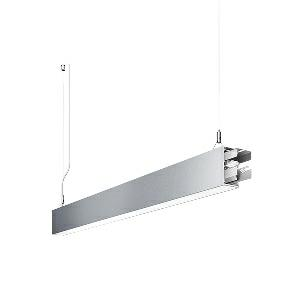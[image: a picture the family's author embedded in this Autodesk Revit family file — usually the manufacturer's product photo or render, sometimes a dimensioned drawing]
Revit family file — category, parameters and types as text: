
# Revit family: idoo_line_-_ilp_4000_840_d_sta_00805699_b23a
name_source: partatom
category: Lighting Fixtures
units: mm (PartAtom-declared; Revit-internal decimal feet)

## family parameters
Cut with Voids When Loaded = No
Host = Face
Light Source = No
Part Type = Normal
Room Calculation Point = No
Round Connector Dimension = Use Diameter
Shared = No

## types (1)
- IDOO.line - ILP 4000/840/D STA (1 x LED, 3950 lm, 4000K)
    Apparent Load = 29 VA
    Approval mark = CE
    CIE Flux Codes = 66 91 98 40 100
    Color Rendering = 80-89
    Color Temperature = 4000K
    Control Gear = Electronic ballast
    Default Elevation = 1800 mm
    Description = ILP 4000/840/D|Suspended luminaire|light source: LED|connected load: 220-240 V, 50/60 Hz|Power consumption: approx. 29 W|standby: approx. 0,15|luminous flux: 3950 lm|luminous efficacy: 136 lm/W|light distribution: Direct/indirect|direct ratio: approx. 40 %|colour temperature: Cold white, ca. 4000 K|color rendering index (CRI): >= 80|chromaticity tolerance:  3 SDCM|System of protection: IP 40|technology: Continuously dimmable|luminaire body|material: Sectional aluminium|colour: Silver|lamp cover: Acrylic (PMMA), Clear|mains lead: 2.00 m With free stranded wires|Fastening: Steel cable 0.3 - 0.7 m|glare control: Prism aperture|luminance(L65): <= 2700 cd/m|unified glare rating(4H 8H): <=  16|special features: DALI Load 1x, TouchDIM - dimming via standard switch, Through-wired, up to 18 m on one mains connection, Flicker-free, Suitable as emergency lighting, Start luminaire with mains connection, Mechanical and electrical connection of the individual modules without tools|
    Frequency = 50 Hz
    Height = 110 mm
    Lamp = 1 x LED
    Lamp Light Flux = 3950 lm
    Lamp count = 1
    Length = 1408 mm
    Luminous efficacy = 136 lm/W
    Manufacturer = Waldmann
    ModVariant = No
    Model = 00805699
    Mounting Place = Ceiling
    Mounting Type = Pendant
    Number of Poles = 1
    OnlyDefault = Yes
    Power Factor = 1
    Product Name = IDOO.line - ILP 4000/840/D STA
    Product group = Suspended luminaire
    ProductGroupID = 9
    Protection Class = Protection class I
    Protection Degree = IP 40
    RLX_Detail_Level = 1
    RLX_Emergency_Light_Flux = 0 lm
    RLX_Emergency_Type = 0
    RLX_Emergency_Type_DB = No
    RlxData = <blob elided: 23437 chars, md5=4621caf4>
    Socket = socket
    Standby Power = 0 W
    System Light Flux = 3950 lm
    System Power = 29 W
    Type Comments = Product without accessories
    Type Image = 113310000-00692594.jpg
    URL = http://relux.com
    VarID = ---
    Voltage = 230 V
    Voltage Range = 220-240 V
    Weight = 0.00 kg
    Width = 60 mm  [stored 0.19685 ft]

note: [stored X ft] marks values corroborated as IEEE doubles in the binary element streams (Revit-internal decimal feet)

## geometry (parser evidence)
native form markers: Blend x4, Sweep x15
no freeform markers — native parametric forms only
